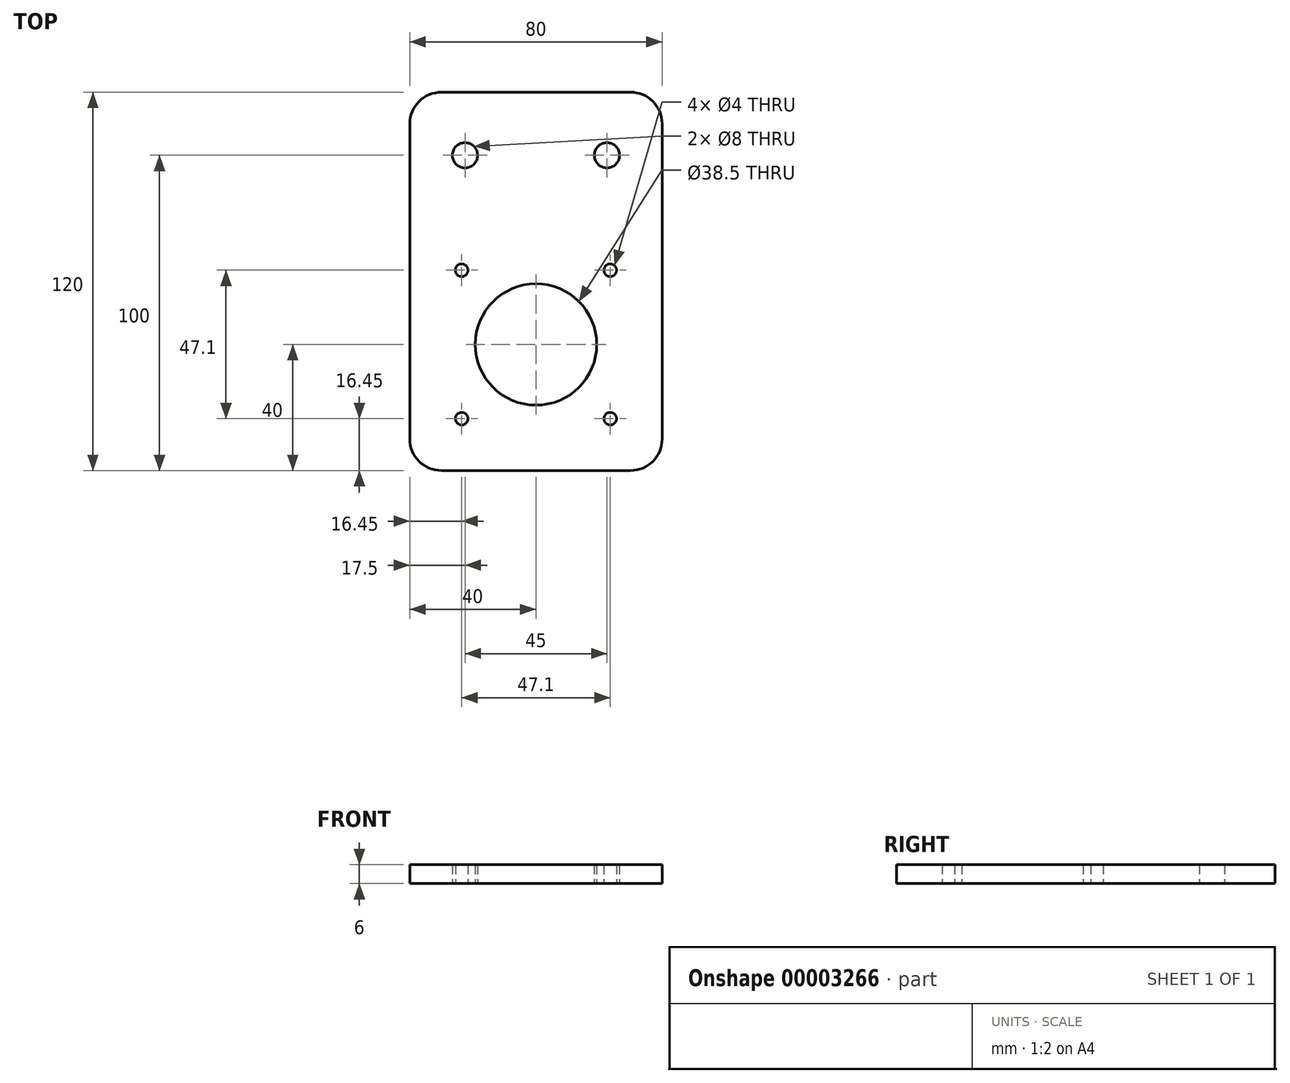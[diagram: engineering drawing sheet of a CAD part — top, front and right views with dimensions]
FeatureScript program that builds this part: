
annotation { "Feature Type Name" : "Feature", "Feature Type Description" : "" }
export const myFeature = defineFeature(function(context is Context, id is Id, definition is map)
    precondition{}
    {
        {
            var Q0;
            Q0=qCreatedBy(makeId("Top.planeOp"),FACE);
            var sketch = newSketch(context, id + "F0", { "sketchPlane" : qUnion([Q0])});
            skCircle(sketch, "E0", {"center": v(0, 0) * mm, "radius": 19.25 * mm});
            skLineSegment(sketch, "E1.bottom", {"start": v(-30, 80) * mm, "end": v(30, 80) * mm});
            skLineSegment(sketch, "E1.top", {"start": v(-30, -40) * mm, "end": v(30, -40) * mm});
            skLineSegment(sketch, "E1.left", {"start": v(-40, 70) * mm, "end": v(-40, -30) * mm});
            skLineSegment(sketch, "E1.right", {"start": v(40, 70) * mm, "end": v(40, -30) * mm});
            skCircle(sketch, "E2", {"center": v(-23.55, 23.55) * mm, "radius": 2 * mm});
            skCircle(sketch, "E3", {"center": v(23.55, 23.55) * mm, "radius": 2 * mm});
            skCircle(sketch, "E4", {"center": v(23.55, -23.55) * mm, "radius": 2 * mm});
            skCircle(sketch, "E5", {"center": v(-23.55, -23.55) * mm, "radius": 2 * mm});
            skCircle(sketch, "E6", {"center": v(-22.5, 60) * mm, "radius": 4 * mm});
            skCircle(sketch, "E7", {"center": v(22.5, 60) * mm, "radius": 4 * mm});
            skPoint(sketch, "E8.visualSharp", {"position": v(40, -40) * mm});
            skArc(sketch, "E8.filletArc", {"start": v(30, -40) * mm, "mid": v(37.07, -37.07) * mm, "end": v(40, -30) * mm});
            skPoint(sketch, "E9.visualSharp", {"position": v(-40, -40) * mm});
            skArc(sketch, "E9.filletArc", {"start": v(-40, -30) * mm, "mid": v(-37.07, -37.07) * mm, "end": v(-30, -40) * mm});
            skPoint(sketch, "E10.visualSharp", {"position": v(-40, 80) * mm});
            skArc(sketch, "E10.filletArc", {"start": v(-30, 80) * mm, "mid": v(-37.07, 77.07) * mm, "end": v(-40, 70) * mm});
            skPoint(sketch, "E11.visualSharp", {"position": v(40, 80) * mm});
            skArc(sketch, "E11.filletArc", {"start": v(40, 70) * mm, "mid": v(37.07, 77.07) * mm, "end": v(30, 80) * mm});
            skLineSegment(sketch, "E12", {"start": v(0, 0) * mm, "end": v(0, 108.85) * mm, "construction": true});
            skSolve(sketch);
        }
        {
            var Q0;
            Q0 = qSketchRegion(id + "F0", true);
            extrude(context, id + "F1", {"entities" : qUnion([Q0]), "depth" : 6 * mm});
        }
    });
